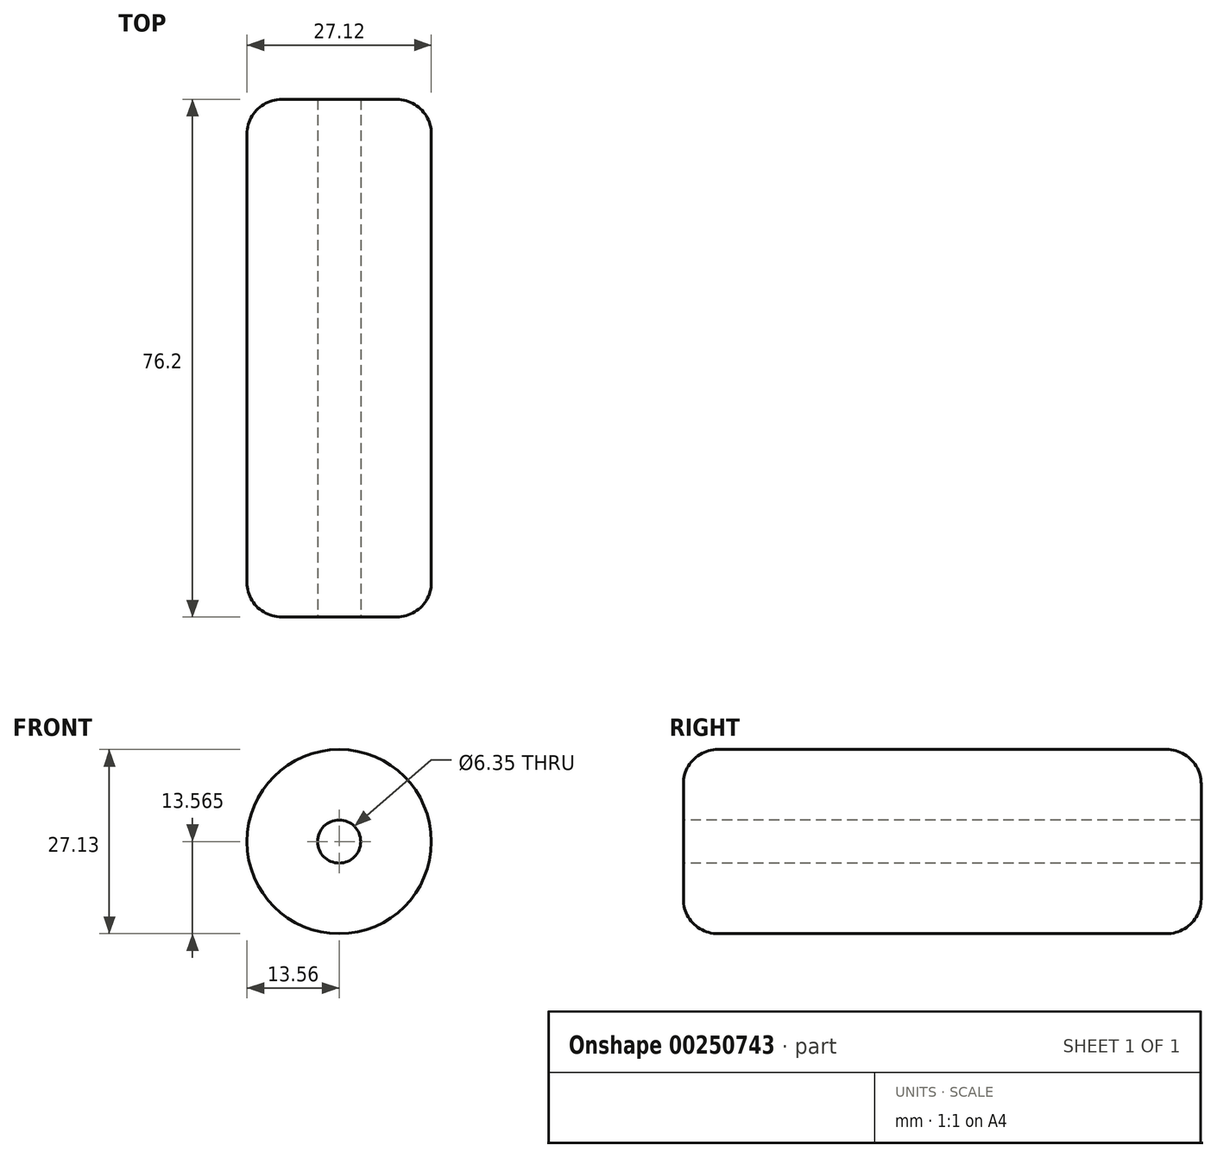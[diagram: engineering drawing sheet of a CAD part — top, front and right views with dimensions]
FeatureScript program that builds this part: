
annotation { "Feature Type Name" : "Feature", "Feature Type Description" : "" }
export const myFeature = defineFeature(function(context is Context, id is Id, definition is map)
    precondition{}
    {
        {
            var Q0;
            Q0=qCreatedBy(makeId("Front.planeOp"),FACE);
            var sketch = newSketch(context, id + "F0", { "sketchPlane" : qUnion([Q0])});
            skCircle(sketch, "E0", {"center": v(-17.78, 21.71) * mm, "radius": 13.56 * mm});
            skSolve(sketch);
        }
        {
            var Q0;
            Q0=makeQuery(id+"F0.imprint","IMPRINT",FACE,{"disambiguationData":[TD([[makeQuery(id+"F0.imprint","IMPRINT",EDGE,{"derivedFrom":sQuery(id+"F0.wireOp",EDGE,"E0")}),1.0]])]});
            extrude(context, id + "F1", {"entities" : qUnion([Q0]), "depth" : 76.2 * mm});
        }
        {
            var Q0;
            Q0=makeQuery(id+"F1.opExtrude","CAP_FACE",FACE,{"disambiguationData":[OSD([sQuery(id+"F0.wireOp",EDGE,"E0")])],"isStart":false});
            var sketch = newSketch(context, id + "F2", { "sketchPlane" : qUnion([Q0])});
            skCircle(sketch, "E1", {"center": v(-17.78, 21.71) * mm, "radius": 7.63 * mm});
            skSolve(sketch);
        }
        {
            var Q0;
            Q0=sQuery(id+"F2.wireOp",VERTEX,"E1.center");
            var Q1;
            Q1=makeQuery(id+"F1.opExtrude","SWEPT_BODY",BODY,{"disambiguationData":[OSD([sQuery(id+"F0.wireOp",EDGE,"E0")])]});
            hole(context, id + "F3", {"style" : HoleStyle.SIMPLE, "endStyle" : HoleEndStyle.THROUGH, "holeDiameter" : 6.35 * mm, "tappedDepth" : 12.7 * mm, "tapClearance" : 3, "locations" : qUnion([Q0]), "scope" : qUnion([Q1])});
        }
        {
            var Q0;
            Q0=makeQuery(id+"F1.opExtrude","CAP_EDGE",EDGE,{"disambiguationData":[OSD([sQuery(id+"F0.wireOp",EDGE,"E0")])],"isStart":false});
            fillet(context, id + "F4", {"entities" : qUnion([Q0]), "radius" : 5.08 * mm, "tangentPropagation" : true, "allowEdgeOverflow" : false});
        }
        {
            var Q0;
            Q0=makeQuery(id+"F1.opExtrude","CAP_EDGE",EDGE,{"disambiguationData":[OSD([sQuery(id+"F0.wireOp",EDGE,"E0")])],"isStart":true});
            fillet(context, id + "F5", {"entities" : qUnion([Q0]), "radius" : 5.08 * mm, "tangentPropagation" : true, "allowEdgeOverflow" : false});
        }
    });
